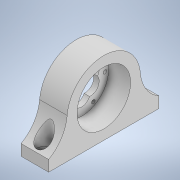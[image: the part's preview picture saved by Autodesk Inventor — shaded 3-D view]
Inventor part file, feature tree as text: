
AUTODESK INVENTOR PART (.ipt)
format: ipt  version: 2020.2 (Build 242310000, 310)  size: 231,424 bytes
history: native  units: in
note: dims shown in document units (in); Inventor stores cm internally (conversion verified against a paired STEP export)
features: extrude x6, sketch x6, fillet x2, projected_geometry x2, hole x1, pattern_circular x1
ambient origin geometry x8: Origin, YZ Plane, XZ Plane, XY Plane, X Axis, Y Axis, Z Axis, Center Point
bodies: Solid1 (feature_tree)
feature tree (18):
  extrude  "Extrusion1"  Depth=3.0in
  extrude  "Extrusion2"  Depth=0.5in
  extrude  "Extrusion3"  Depth=1.0in
  fillet  "Fillet1"  Radius=1.7in
  sketch  "Sketch6"  dims[d10=1.46in d11=0.6in d12=0.0in]
  fillet  "Fillet2"  Radius=1.0in
  hole  "Hole1"  [1 undecoded]
  extrude  "Extrusion5"  Depth=1.0in
  extrude  "Extrusion8"  Depth=1.0in
  pattern_circular  "Circular Pattern4"  [2 undecoded]
  extrude  "Extrusion10"  Depth=1.0in
  sketch  "Sketch1"  dims[d0=0.75in d1=3.0in]
  sketch  "Sketch2"  dims[d2=0.3in d3=0.0in d4=0.5in]
  sketch  "Sketch3"  dims[d5=0.75in d6=2.0in d7=1.7in d8=0.0in d9=1.0in]
  sketch  "Sketch7"  dims[d19=1.0in d20=0.25in]
  projected_geometry  "Projected Loop1"
  sketch  "Sketch14"  dims[d21=0.25in d22=1.0in d23=0.2in d24=0.75in d25=0.4in d26=0.15in d27=0.5635in d28=1.0in d29=0.8108in d30=0.4in d31=0.4in d32=0.6in d33=0.0in d66=1.0in d67=0.0in d92=2.3622in d93=360.0deg d95=1.0in d96=0.0in]
  projected_geometry  "Projected Loop2"
note: 3 required parameter values undecoded (feature->parameter linkage not recoverable at this tier; creation-order binding heuristic only, values carry confidence <= 0.55)
